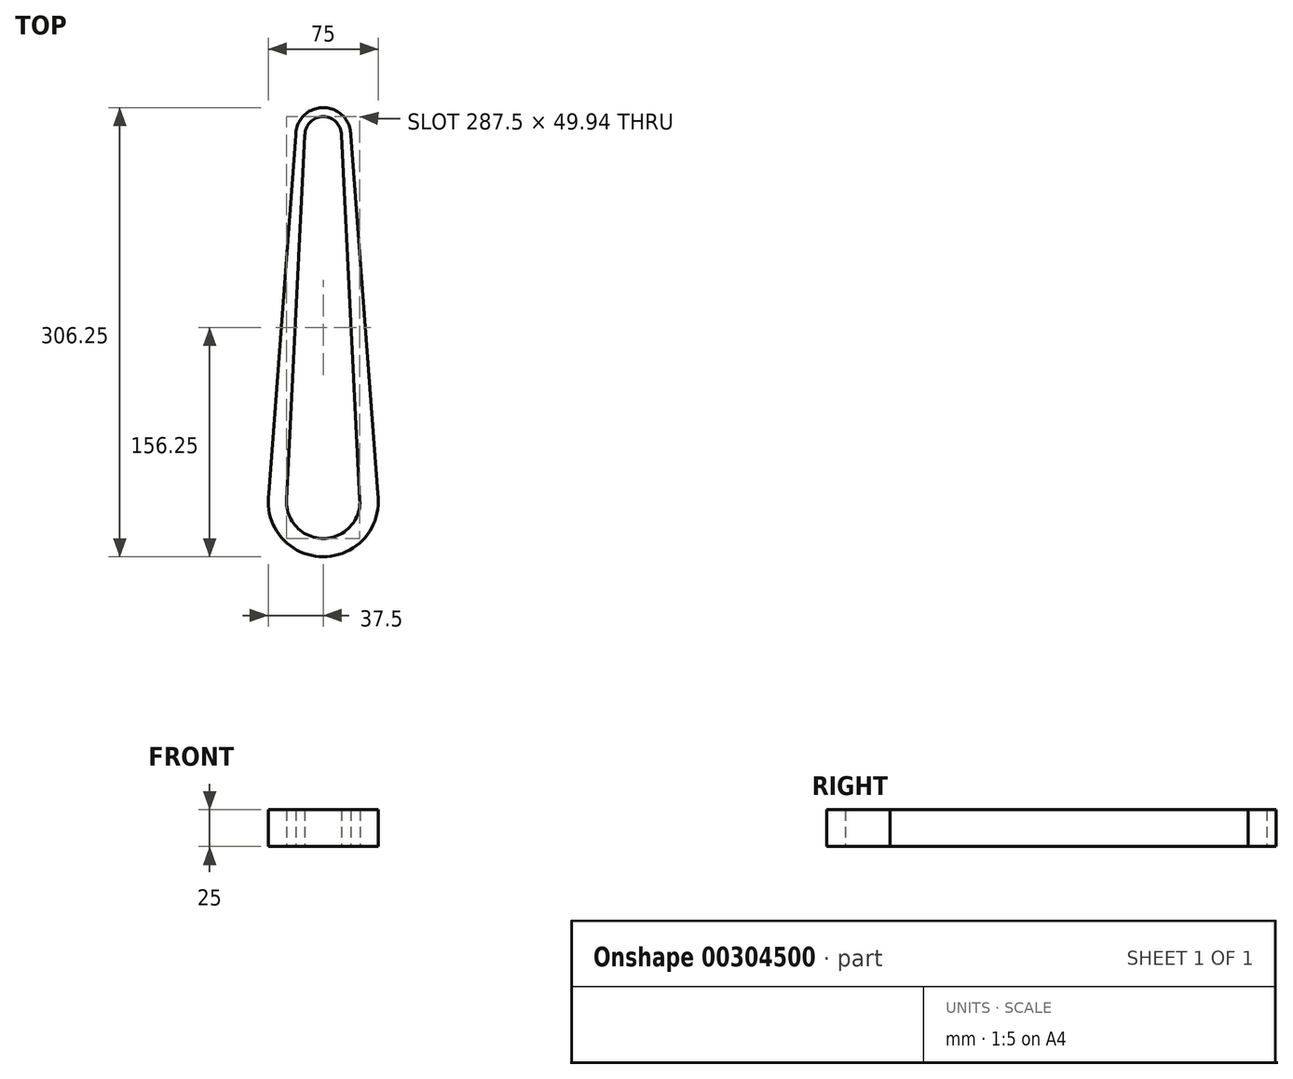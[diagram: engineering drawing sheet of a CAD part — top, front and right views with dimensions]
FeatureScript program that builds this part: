
annotation { "Feature Type Name" : "Feature", "Feature Type Description" : "" }
export const myFeature = defineFeature(function(context is Context, id is Id, definition is map)
    precondition{}
    {
        {
            var Q0;
            Q0=qCreatedBy(makeId("Top.planeOp"),FACE);
            var sketch = newSketch(context, id + "F0", { "sketchPlane" : qUnion([Q0])});
            skCircle(sketch, "E0", {"center": v(0, 0) * mm, "radius": 12.5 * mm});
            skCircle(sketch, "E1", {"center": v(0, 0) * mm, "radius": 25 * mm});
            skLineSegment(sketch, "E2", {"start": v(0, 0) * mm, "end": v(0, 250) * mm});
            skLineSegment(sketch, "E3", {"start": v(-12.5, 250) * mm, "end": v(12.5, 250) * mm, "construction": true});
            skLineSegment(sketch, "E4", {"start": v(-12.5, 250) * mm, "end": v(-12.5, 0) * mm, "construction": true});
            skCircle(sketch, "E5", {"center": v(0, 250) * mm, "radius": 12.5 * mm});
            skLineSegment(sketch, "E6", {"start": v(-12.5, 250) * mm, "end": v(-24.97, 1.25) * mm});
            skLineSegment(sketch, "E7", {"start": v(12.5, 250) * mm, "end": v(24.97, 1.25) * mm});
            skCircle(sketch, "E8", {"center": v(0, 250) * mm, "radius": 18.75 * mm});
            skCircle(sketch, "E9", {"center": v(0, 0) * mm, "radius": 37.5 * mm});
            skLineSegment(sketch, "E10", {"start": v(-37.5, 0) * mm, "end": v(-18.75, 250) * mm});
            skLineSegment(sketch, "E11", {"start": v(37.5, 0) * mm, "end": v(18.73, 250) * mm});
            skPoint(sketch, "E11.endSnap0", {"position": v(18.73, 125.63) * mm});
            skSolve(sketch);
        }
        {
            var Q0;
            Q0 = qSketchRegion(id + "F0", true);
            extrude(context, id + "F1", {"entities" : qUnion([Q0]), "depth" : 25 * mm, "symmetric" : true});
        }
    });
